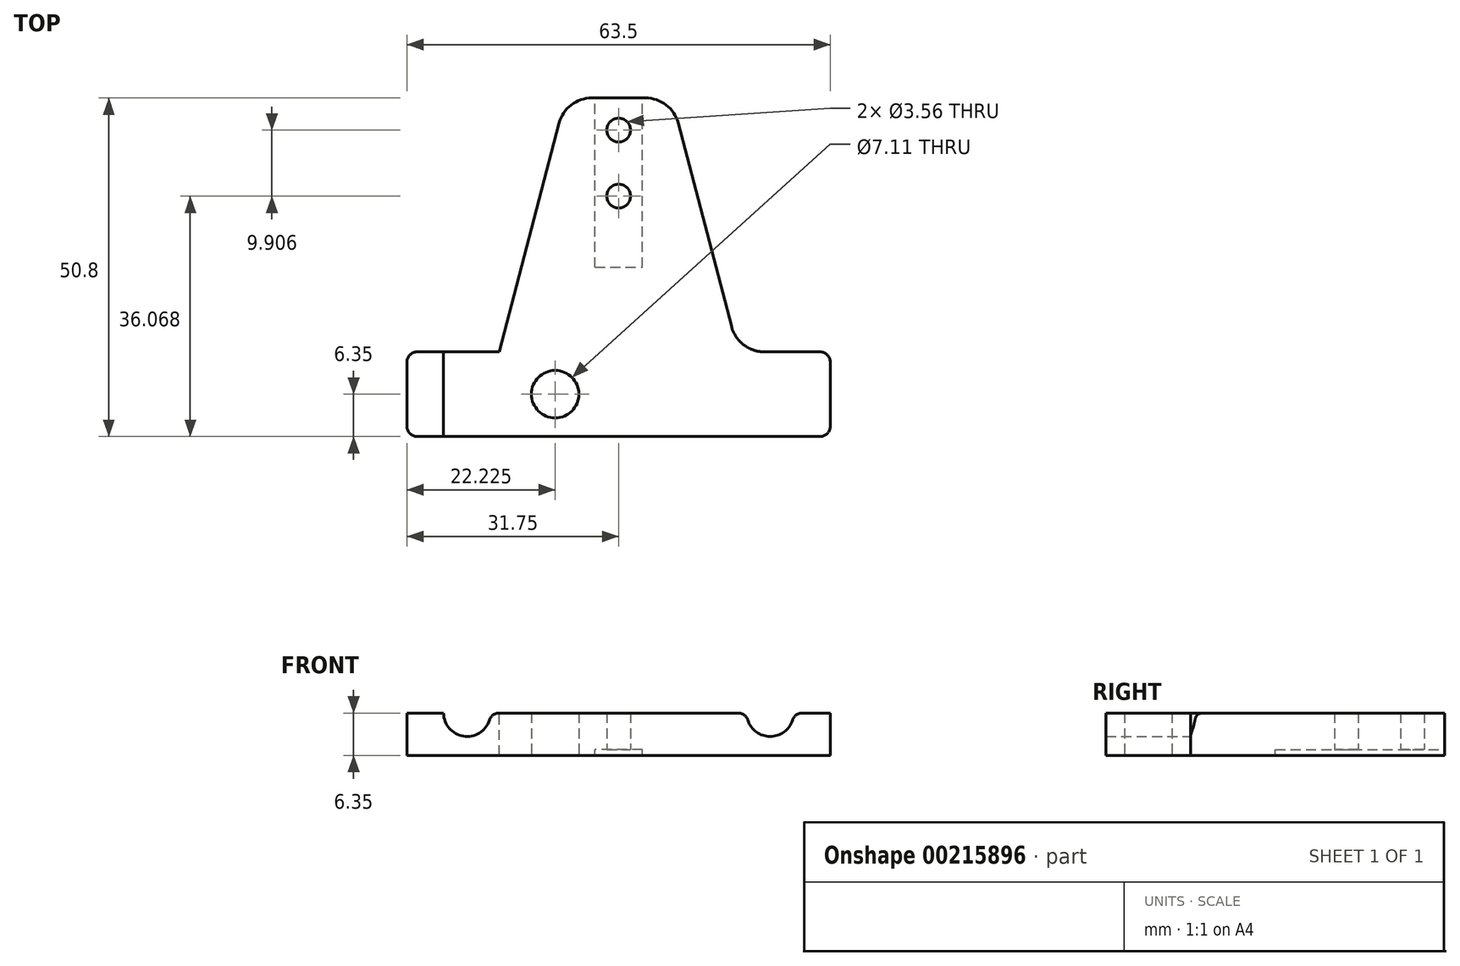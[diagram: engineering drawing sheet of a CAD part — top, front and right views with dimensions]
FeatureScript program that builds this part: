
annotation { "Feature Type Name" : "Feature", "Feature Type Description" : "" }
export const myFeature = defineFeature(function(context is Context, id is Id, definition is map)
    precondition{}
    {
        {
            var Q0;
            Q0=qCreatedBy(makeId("Top.planeOp"),FACE);
            var sketch = newSketch(context, id + "F0", { "sketchPlane" : qUnion([Q0])});
            skLineSegment(sketch, "E0", {"start": v(-31.75, 0) * mm, "end": v(-31.75, -12.7) * mm});
            skLineSegment(sketch, "E1", {"start": v(-31.75, -12.7) * mm, "end": v(0, -12.7) * mm});
            skLineSegment(sketch, "E2", {"start": v(-31.75, 0) * mm, "end": v(0, 0) * mm});
            skLineSegment(sketch, "E3.MirrorCS", {"start": v(31.75, 0) * mm, "end": v(0, 0) * mm});
            skLineSegment(sketch, "E4.MirrorCS", {"start": v(31.75, -12.7) * mm, "end": v(0, -12.7) * mm});
            skLineSegment(sketch, "E5.MirrorCS", {"start": v(31.75, 0) * mm, "end": v(31.75, -12.7) * mm});
            skSolve(sketch);
        }
        {
            var Q0;
            Q0 = qSketchRegion(id + "F0", true);
            extrude(context, id + "F1", {"entities" : qUnion([Q0]), "depth" : 6.35 * mm});
        }
        {
            var Q0;
            Q0=makeQuery(id+"F1.opExtrude","SWEPT_FACE",FACE,{"disambiguationData":[OSD([sQuery(id+"F0.wireOp",EDGE,"E2"),sQuery(id+"F0.wireOp",EDGE,"E3.MirrorCS")])]});
            var sketch = newSketch(context, id + "F2", { "sketchPlane" : qUnion([Q0])});
            skCircle(sketch, "E6", {"center": v(-22.73, 6.35) * mm, "radius": 3.52 * mm});
            skCircle(sketch, "E7", {"center": v(22.73, 6.35) * mm, "radius": 3.52 * mm});
            skSolve(sketch);
        }
        {
            var Q0;
            Q0 = qSketchRegion(id + "F2", true);
            extrude(context, id + "F3", {"entities" : qUnion([Q0]), "operationType" : NewBodyOperationType.REMOVE, "endBound" : BoundingType.UP_TO_NEXT, "oppositeDirection" : true, "depth" : 25.4 * mm});
        }
        {
            var Q0;
            Q0=makeQuery(id+"F1.opExtrude","SWEPT_EDGE",EDGE,{"disambiguationData":[OSD([sQuery(id+"F0.wireOp",EDGE,"E3.MirrorCS"),sQuery(id+"F0.wireOp",EDGE,"E5.MirrorCS")])]});
            var Q1;
            Q1=makeQuery(id+"F1.opExtrude","SWEPT_EDGE",EDGE,{"disambiguationData":[OSD([sQuery(id+"F0.wireOp",EDGE,"E4.MirrorCS"),sQuery(id+"F0.wireOp",EDGE,"E5.MirrorCS")])]});
            var Q2;
            Q2=makeQuery(id+"F1.opExtrude","SWEPT_EDGE",EDGE,{"disambiguationData":[OSD([sQuery(id+"F0.wireOp",EDGE,"E0"),sQuery(id+"F0.wireOp",EDGE,"E2")])]});
            var Q3;
            Q3=makeQuery(id+"F1.opExtrude","SWEPT_EDGE",EDGE,{"disambiguationData":[OSD([sQuery(id+"F0.wireOp",EDGE,"E0"),sQuery(id+"F0.wireOp",EDGE,"E1")])]});
            var Q4;
            {var subQ0=sQuery(id+"F0.wireOp",EDGE,"E3.MirrorCS");var subQ1=sQuery(id+"F0.wireOp",EDGE,"E2");var subQ2=sQuery(id+"F2.wireOp",EDGE,"E6");var subQ3=makeQuery(id+"F1.opExtrude","CAP_EDGE",EDGE,{"disambiguationData":[OSD([subQ1,subQ0])],"isStart":false});var subQ4=makeQuery(id+"F2.imprint","INTERSECT",VERTEX,{"disambiguationData":[OD(0.0)],"derivedFrom":[subQ3,subQ2]});Q4=makeQuery(id+"F3.boolean.opBoolean","COPY",EDGE,{"derivedFrom":makeQuery(id+"F3.opExtrude","CAP_EDGE",EDGE,{"disambiguationData":[OSD([subQ2]),topologyDisambiguationEdgeConnected([makeQuery(id+"F1.opExtrude","CAP_FACE",FACE,{"disambiguationData":[OSD([sQuery(id+"F0.wireOp",EDGE,"E0"),sQuery(id+"F0.wireOp",EDGE,"E1"),subQ1,subQ0,sQuery(id+"F0.wireOp",EDGE,"E4.MirrorCS"),sQuery(id+"F0.wireOp",EDGE,"E5.MirrorCS")])],"isStart":false}),makeQuery(id+"F2.imprint","IMPRINT",EDGE,{"disambiguationData":[TD([[subQ4,1.0]])],"derivedFrom":subQ2}),makeQuery(id+"F2.imprint","IMPRINT",EDGE,{"disambiguationData":[TD([[subQ4,-1.0]])],"derivedFrom":subQ2})]),OD(1.0)],"isStart":false})});}
            var Q5;
            {var subQ0=sQuery(id+"F0.wireOp",EDGE,"E3.MirrorCS");var subQ1=sQuery(id+"F0.wireOp",EDGE,"E2");var subQ2=sQuery(id+"F2.wireOp",EDGE,"E6");var subQ3=makeQuery(id+"F1.opExtrude","CAP_EDGE",EDGE,{"disambiguationData":[OSD([subQ1,subQ0])],"isStart":false});var subQ4=makeQuery(id+"F2.imprint","INTERSECT",VERTEX,{"disambiguationData":[OD(0.0)],"derivedFrom":[subQ3,subQ2]});Q5=makeQuery(id+"F3.boolean.opBoolean","COPY",EDGE,{"derivedFrom":makeQuery(id+"F3.opExtrude","CAP_EDGE",EDGE,{"disambiguationData":[OSD([subQ2]),topologyDisambiguationEdgeConnected([makeQuery(id+"F1.opExtrude","CAP_FACE",FACE,{"disambiguationData":[OSD([sQuery(id+"F0.wireOp",EDGE,"E0"),sQuery(id+"F0.wireOp",EDGE,"E1"),subQ1,subQ0,sQuery(id+"F0.wireOp",EDGE,"E4.MirrorCS"),sQuery(id+"F0.wireOp",EDGE,"E5.MirrorCS")])],"isStart":false}),makeQuery(id+"F2.imprint","IMPRINT",EDGE,{"disambiguationData":[TD([[subQ4,1.0]])],"derivedFrom":subQ2}),makeQuery(id+"F2.imprint","IMPRINT",EDGE,{"disambiguationData":[TD([[subQ4,-1.0]])],"derivedFrom":subQ2})]),OD(0.0)],"isStart":false})});}
            var Q6;
            Q6=makeQuery(id+"F3.boolean.opBoolean","COPY",EDGE,{"derivedFrom":makeQuery(id+"F3.opExtrude","CAP_EDGE",EDGE,{"disambiguationData":[OSD([sQuery(id+"F2.wireOp",EDGE,"E7")]),topologyDisambiguationEdgeConnected([makeQuery(id+"F1.opExtrude","CAP_FACE",FACE,{"disambiguationData":[OSD([sQuery(id+"F0.wireOp",EDGE,"E0"),sQuery(id+"F0.wireOp",EDGE,"E1"),sQuery(id+"F0.wireOp",EDGE,"E2"),sQuery(id+"F0.wireOp",EDGE,"E3.MirrorCS"),sQuery(id+"F0.wireOp",EDGE,"E4.MirrorCS"),sQuery(id+"F0.wireOp",EDGE,"E5.MirrorCS")])],"isStart":false})]),OD(1.0)],"isStart":false})});
            var Q7;
            Q7=makeQuery(id+"F3.boolean.opBoolean","COPY",EDGE,{"derivedFrom":makeQuery(id+"F3.opExtrude","CAP_EDGE",EDGE,{"disambiguationData":[OSD([sQuery(id+"F2.wireOp",EDGE,"E7")]),topologyDisambiguationEdgeConnected([makeQuery(id+"F1.opExtrude","CAP_FACE",FACE,{"disambiguationData":[OSD([sQuery(id+"F0.wireOp",EDGE,"E0"),sQuery(id+"F0.wireOp",EDGE,"E1"),sQuery(id+"F0.wireOp",EDGE,"E2"),sQuery(id+"F0.wireOp",EDGE,"E3.MirrorCS"),sQuery(id+"F0.wireOp",EDGE,"E4.MirrorCS"),sQuery(id+"F0.wireOp",EDGE,"E5.MirrorCS")])],"isStart":false})]),OD(0.0)],"isStart":false})});
            fillet(context, id + "F4", {"entities" : qUnion([Q0, Q1, Q2, Q3, Q4, Q5, Q6, Q7]), "radius" : 1.52 * mm, "tangentPropagation" : true, "allowEdgeOverflow" : false});
        }
        {
            var Q0;
            {var subQ0=sQuery(id+"F0.wireOp",EDGE,"E4.MirrorCS");var subQ1=sQuery(id+"F0.wireOp",EDGE,"E1");var subQ2=sQuery(id+"F0.wireOp",EDGE,"E3.MirrorCS");var subQ3=sQuery(id+"F0.wireOp",EDGE,"E2");Q0=makeQuery(id+"F3.boolean.opBoolean","SPLIT",FACE,{"disambiguationData":[TD([makeQuery(id+"F1.opExtrude","SWEPT_FACE",FACE,{"disambiguationData":[OSD([subQ1,subQ0])]}),makeQuery(id+"F1.opExtrude","SWEPT_FACE",FACE,{"disambiguationData":[OSD([subQ3,subQ2])]}),makeQuery(id+"F3.opExtrude","SWEPT_FACE",FACE,{"disambiguationData":[OSD([sQuery(id+"F2.wireOp",EDGE,"E6")])]}),makeQuery(id+"F3.opExtrude","SWEPT_FACE",FACE,{"disambiguationData":[OSD([sQuery(id+"F2.wireOp",EDGE,"E7")])]})])],"derivedFrom":makeQuery(id+"F1.opExtrude","CAP_FACE",FACE,{"disambiguationData":[OSD([sQuery(id+"F0.wireOp",EDGE,"E0"),subQ1,subQ3,subQ2,subQ0,sQuery(id+"F0.wireOp",EDGE,"E5.MirrorCS")])],"isStart":false})});}
            var sketch = newSketch(context, id + "F5", { "sketchPlane" : qUnion([Q0])});
            skLineSegment(sketch, "E8", {"start": v(-17.93, 0) * mm, "end": v(-7.94, 38.1) * mm});
            skLineSegment(sketch, "E9", {"start": v(-7.94, 38.1) * mm, "end": v(0, 38.1) * mm});
            skLineSegment(sketch, "E10", {"start": v(0, 0) * mm, "end": v(-17.93, 0) * mm});
            skLineSegment(sketch, "E11.MirrorCS", {"start": v(17.93, 0) * mm, "end": v(7.94, 38.1) * mm});
            skLineSegment(sketch, "E12.MirrorCS", {"start": v(0, 0) * mm, "end": v(17.93, 0) * mm});
            skLineSegment(sketch, "E13.MirrorCS", {"start": v(7.94, 38.1) * mm, "end": v(0, 38.1) * mm});
            skSolve(sketch);
        }
        {
            var Q0;
            Q0 = qSketchRegion(id + "F5", true);
            var Q1;
            Q1=makeQuery(id+"F1.opExtrude","CAP_FACE",FACE,{"disambiguationData":[OSD([sQuery(id+"F0.wireOp",EDGE,"E0"),sQuery(id+"F0.wireOp",EDGE,"E1"),sQuery(id+"F0.wireOp",EDGE,"E2"),sQuery(id+"F0.wireOp",EDGE,"E3.MirrorCS"),sQuery(id+"F0.wireOp",EDGE,"E4.MirrorCS"),sQuery(id+"F0.wireOp",EDGE,"E5.MirrorCS")])],"isStart":true});
            extrude(context, id + "F6", {"entities" : qUnion([Q0]), "operationType" : NewBodyOperationType.ADD, "endBound" : BoundingType.UP_TO_SURFACE, "oppositeDirection" : true, "endBoundEntityFace" : qUnion([Q1]), "depth" : 25.4 * mm});
        }
        {
            var Q0;
            Q0=makeQuery(id+"F6.opExtrude","SWEPT_EDGE",EDGE,{"disambiguationData":[OSD([sQuery(id+"F0.wireOp",EDGE,"E0"),sQuery(id+"F0.wireOp",EDGE,"E1"),sQuery(id+"F0.wireOp",EDGE,"E2"),sQuery(id+"F0.wireOp",EDGE,"E3.MirrorCS"),sQuery(id+"F0.wireOp",EDGE,"E4.MirrorCS"),sQuery(id+"F0.wireOp",EDGE,"E5.MirrorCS"),sQuery(id+"F2.wireOp",EDGE,"E6"),sQuery(id+"F5.wireOp",EDGE,"E11.MirrorCS"),sQuery(id+"F5.wireOp",EDGE,"E12.MirrorCS")])]});
            var Q1;
            Q1=makeQuery(id+"F6.opExtrude","SWEPT_EDGE",EDGE,{"disambiguationData":[OSD([sQuery(id+"F0.wireOp",EDGE,"E0"),sQuery(id+"F0.wireOp",EDGE,"E1"),sQuery(id+"F0.wireOp",EDGE,"E2"),sQuery(id+"F0.wireOp",EDGE,"E3.MirrorCS"),sQuery(id+"F0.wireOp",EDGE,"E4.MirrorCS"),sQuery(id+"F0.wireOp",EDGE,"E5.MirrorCS"),sQuery(id+"F2.wireOp",EDGE,"E7"),sQuery(id+"F5.wireOp",EDGE,"E8"),sQuery(id+"F5.wireOp",EDGE,"E10")])]});
            var Q2;
            Q2=makeQuery(id+"F6.opExtrude","SWEPT_EDGE",EDGE,{"disambiguationData":[OSD([sQuery(id+"F5.wireOp",EDGE,"E11.MirrorCS"),sQuery(id+"F5.wireOp",EDGE,"E13.MirrorCS")])]});
            var Q3;
            Q3=makeQuery(id+"F6.opExtrude","SWEPT_EDGE",EDGE,{"disambiguationData":[OSD([sQuery(id+"F5.wireOp",EDGE,"E8"),sQuery(id+"F5.wireOp",EDGE,"E9")])]});
            fillet(context, id + "F7", {"entities" : qUnion([Q0, Q1, Q2, Q3]), "radius" : 5.08 * mm, "tangentPropagation" : true, "allowEdgeOverflow" : false});
        }
        {
            var Q0;
            Q0=makeQuery(id+"F6.opExtrude","SWEPT_FACE",FACE,{"disambiguationData":[OSD([sQuery(id+"F5.wireOp",EDGE,"E9"),sQuery(id+"F5.wireOp",EDGE,"E13.MirrorCS")])]});
            var sketch = newSketch(context, id + "F8", { "sketchPlane" : qUnion([Q0])});
            skLineSegment(sketch, "E14.bottom", {"start": v(-3.56, 0) * mm, "end": v(3.56, 0) * mm});
            skLineSegment(sketch, "E14.top", {"start": v(-3.56, 0.89) * mm, "end": v(3.56, 0.89) * mm});
            skLineSegment(sketch, "E14.left", {"start": v(-3.56, 0) * mm, "end": v(-3.56, 0.89) * mm});
            skLineSegment(sketch, "E14.right", {"start": v(3.56, 0) * mm, "end": v(3.56, 0.89) * mm});
            skSolve(sketch);
        }
        {
            var Q0;
            Q0 = qSketchRegion(id + "F8", true);
            extrude(context, id + "F9", {"entities" : qUnion([Q0]), "operationType" : NewBodyOperationType.REMOVE, "oppositeDirection" : true, "depth" : 25.4 * mm});
        }
        {
            var Q0;
            Q0=makeQuery(id+"F9.boolean.opBoolean","COPY",FACE,{"derivedFrom":makeQuery(id+"F9.opExtrude","SWEPT_FACE",FACE,{"disambiguationData":[OSD([sQuery(id+"F8.wireOp",EDGE,"E14.top")])]})});
            var sketch = newSketch(context, id + "F10", { "sketchPlane" : qUnion([Q0])});
            skCircle(sketch, "E15", {"center": v(0, -33.27) * mm, "radius": 1.78 * mm});
            skCircle(sketch, "E16", {"center": v(0, -23.37) * mm, "radius": 1.78 * mm});
            skSolve(sketch);
        }
        {
            var Q0;
            Q0 = qSketchRegion(id + "F10", true);
            extrude(context, id + "F11", {"entities" : qUnion([Q0]), "operationType" : NewBodyOperationType.REMOVE, "endBound" : BoundingType.UP_TO_NEXT, "oppositeDirection" : true, "depth" : 25.4 * mm});
        }
        {
            var Q0;
            Q0=makeQuery(id+"F6.boolean.opBoolean","MERGE",FACE,{"derivedFrom":[makeQuery(id+"F1.opExtrude","CAP_FACE",FACE,{"disambiguationData":[OSD([sQuery(id+"F0.wireOp",EDGE,"E0"),sQuery(id+"F0.wireOp",EDGE,"E1"),sQuery(id+"F0.wireOp",EDGE,"E2"),sQuery(id+"F0.wireOp",EDGE,"E3.MirrorCS"),sQuery(id+"F0.wireOp",EDGE,"E4.MirrorCS"),sQuery(id+"F0.wireOp",EDGE,"E5.MirrorCS")])],"isStart":true}),makeQuery(id+"F6.opExtrude","CAP_FACE",FACE,{"disambiguationData":[OSD([sQuery(id+"F5.wireOp",EDGE,"E8"),sQuery(id+"F5.wireOp",EDGE,"E9"),sQuery(id+"F5.wireOp",EDGE,"E10"),sQuery(id+"F5.wireOp",EDGE,"E11.MirrorCS"),sQuery(id+"F5.wireOp",EDGE,"E12.MirrorCS"),sQuery(id+"F5.wireOp",EDGE,"E13.MirrorCS")])],"isStart":false})]});
            var sketch = newSketch(context, id + "F12", { "sketchPlane" : qUnion([Q0])});
            skCircle(sketch, "E17", {"center": v(-9.53, 6.35) * mm, "radius": 3.56 * mm});
            skSolve(sketch);
        }
        {
            var Q0;
            Q0 = qSketchRegion(id + "F12", true);
            extrude(context, id + "F13", {"entities" : qUnion([Q0]), "operationType" : NewBodyOperationType.REMOVE, "endBound" : BoundingType.UP_TO_NEXT, "oppositeDirection" : true, "depth" : 25.4 * mm});
        }
    });
